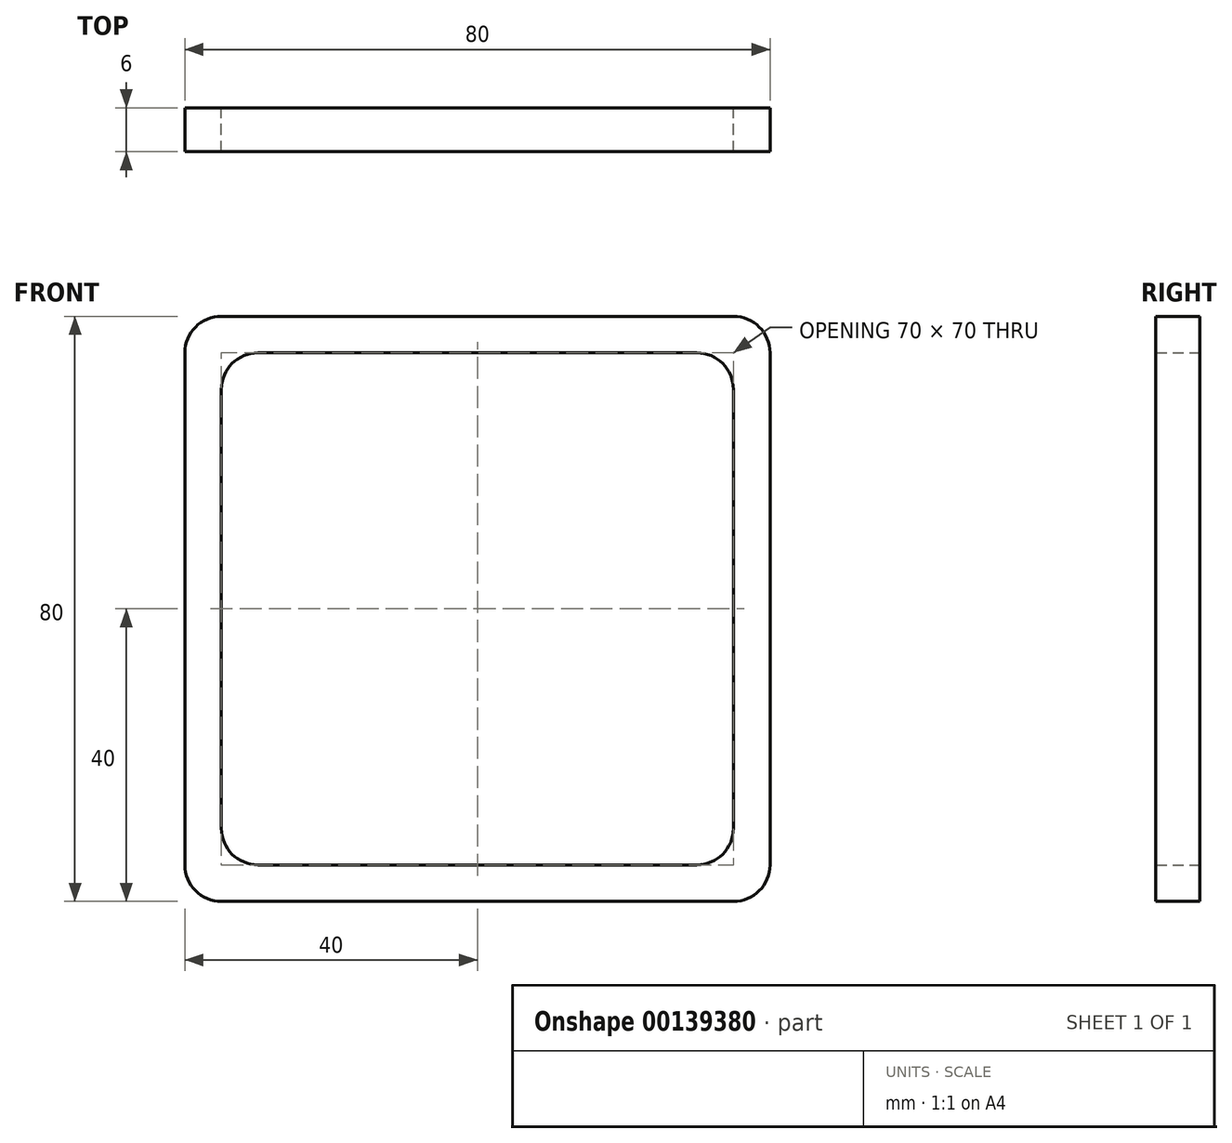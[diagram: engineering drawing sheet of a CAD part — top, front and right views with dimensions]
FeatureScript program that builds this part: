
annotation { "Feature Type Name" : "Feature", "Feature Type Description" : "" }
export const myFeature = defineFeature(function(context is Context, id is Id, definition is map)
    precondition{}
    {
        {
            var Q0;
            Q0=qCreatedBy(makeId("Front.planeOp"),FACE);
            var sketch = newSketch(context, id + "F0", { "sketchPlane" : qUnion([Q0])});
            skLineSegment(sketch, "E0.bottom", {"start": v(-5, 0) * mm, "end": v(-75, 0) * mm});
            skLineSegment(sketch, "E0.top", {"start": v(-5, 80) * mm, "end": v(-75, 80) * mm});
            skLineSegment(sketch, "E0.left", {"start": v(0, 5) * mm, "end": v(0, 75) * mm});
            skLineSegment(sketch, "E0.right", {"start": v(-80, 5) * mm, "end": v(-80, 75) * mm});
            skPoint(sketch, "E1.visualSharp", {"position": v(-80, 80) * mm});
            skArc(sketch, "E1.filletArc", {"start": v(-75, 80) * mm, "mid": v(-78.54, 78.54) * mm, "end": v(-80, 75) * mm});
            skPoint(sketch, "E2.visualSharp", {"position": v(0, 80) * mm});
            skArc(sketch, "E2.filletArc", {"start": v(0, 75) * mm, "mid": v(-1.46, 78.54) * mm, "end": v(-5, 80) * mm});
            skPoint(sketch, "E3.visualSharp", {"position": v(-80, 0) * mm});
            skArc(sketch, "E3.filletArc", {"start": v(-80, 5) * mm, "mid": v(-78.54, 1.46) * mm, "end": v(-75, 0) * mm});
            skPoint(sketch, "E4.visualSharp", {"position": v(0, 0) * mm});
            skArc(sketch, "E4.filletArc", {"start": v(-5, 0) * mm, "mid": v(-1.46, 1.46) * mm, "end": v(0, 5) * mm});
            skLineSegment(sketch, "E5.bottom", {"start": v(-70, 75) * mm, "end": v(-10, 75) * mm});
            skLineSegment(sketch, "E5.top", {"start": v(-70, 5) * mm, "end": v(-10, 5) * mm});
            skLineSegment(sketch, "E5.left", {"start": v(-75, 70) * mm, "end": v(-75, 10) * mm});
            skLineSegment(sketch, "E5.right", {"start": v(-5, 70) * mm, "end": v(-5, 10) * mm});
            skArc(sketch, "E6.filletArc", {"start": v(-70, 75) * mm, "mid": v(-73.54, 73.54) * mm, "end": v(-75, 70) * mm});
            skArc(sketch, "E7.filletArc", {"start": v(-5, 70) * mm, "mid": v(-6.46, 73.54) * mm, "end": v(-10, 75) * mm});
            skArc(sketch, "E8.filletArc", {"start": v(-10, 5) * mm, "mid": v(-6.46, 6.46) * mm, "end": v(-5, 10) * mm});
            skArc(sketch, "E9.filletArc", {"start": v(-75, 10) * mm, "mid": v(-73.54, 6.46) * mm, "end": v(-70, 5) * mm});
            skSolve(sketch);
        }
        {
            var Q0;
            Q0=makeQuery(id+"F0.imprint","IMPRINT",FACE,{"disambiguationData":[TD([[makeQuery(id+"F0.imprint","IMPRINT",EDGE,{"derivedFrom":sQuery(id+"F0.wireOp",EDGE,"E0.bottom")}),-1.0]])]});
            extrude(context, id + "F1", {"entities" : qUnion([Q0]), "depth" : 6 * mm});
        }
    });
